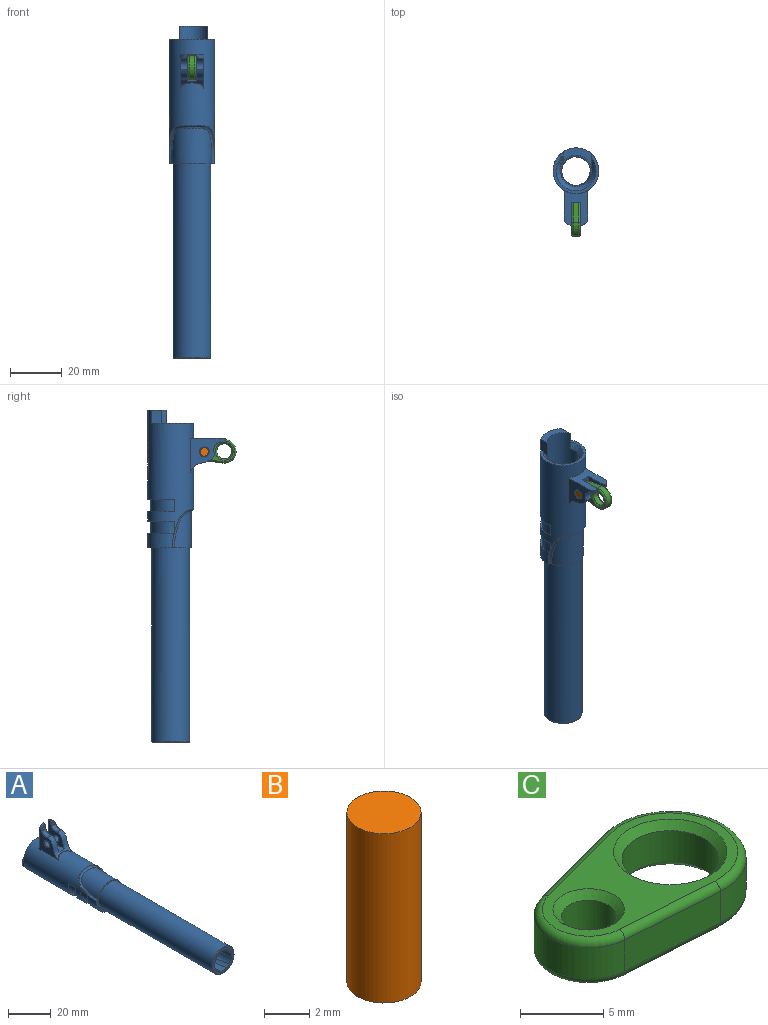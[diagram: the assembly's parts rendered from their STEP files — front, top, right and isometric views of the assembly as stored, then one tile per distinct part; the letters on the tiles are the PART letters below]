
ASSEMBLY  parts=3 mates=2
PART A: 333 faces, bbox 31.5x130.4x32.7 mm
  f0: bspline ~95.71x9.97mm, area 220mm2, adj f16,f17,f18,f23
  f1: bspline ~95.71x9.42mm, area 220mm2, adj f14,f15,f22,f23
  f2: bspline ~95.71x9.97mm, area 220mm2, adj f11,f12,f13,f23
  f3: bspline ~95.71x11mm, area 220mm2, adj f8,f9,f10,f23
  f4: bspline ~95.71x9.42mm, area 220mm2, adj f19,f20,f21,f23
  f5: bspline ~95.71x11mm, area 220mm2, adj f23,f24,f25,f26
  f6: bspline ~14.67x14.67mm, area 9.1mm2, adj f7,f23,f39
  f7: bspline ~14.67x14.67mm, area 9.1mm2, adj f6,f23,f39
  f8: bspline ~95.71x9.97mm, area 14.2mm2, adj f3,f9,f23,f42
  f9: plane 1.95x1.39mm, normal (0,-1,0), area 0.3mm2, adj f3,f8,f10,f42
  f10: bspline ~95.71x9.72mm, area 14.2mm2, adj f3,f9,f23,f42
  f11: bspline ~95.71x8mm, area 14.2mm2, adj f2,f12,f23,f42,f44
  f12: plane 2.28x0.36mm, normal (0,-1,0), area 0.3mm2, adj f2,f11,f13,f42
  f13: bspline ~95.71x9.71mm, area 14.2mm2, adj f2,f12,f23,f42,f43
  f14: bspline ~95.71x9.3mm, area 14.2mm2, adj f1,f15,f23,f42,f43
  f15: plane 2.1x1.12mm, normal (0,-1,0), area 0.3mm2, adj f1,f14,f22,f42
  f16: bspline ~95.71x8mm, area 14.2mm2, adj f0,f17,f23,f42
  f17: plane 2.28x0.36mm, normal (0,-1,0), area 0.3mm2, adj f0,f16,f18,f42
  f18: bspline ~95.71x9.71mm, area 14.2mm2, adj f0,f17,f23,f42
  f19: bspline ~95.71x9.3mm, area 14.2mm2, adj f4,f20,f23,f42
  f20: plane 2.1x1.12mm, normal (0,-1,0), area 0.3mm2, adj f4,f19,f21,f42
  f21: bspline ~95.71x7.31mm, area 14.2mm2, adj f4,f20,f23,f42
  f22: bspline ~95.71x7.31mm, area 14.2mm2, adj f1,f15,f23,f42
  f23: plane 14.17x14.17mm, normal (0,-1,0), area 53mm2, adj f0,f1,f2,f3,f4,f5,f6,f7
  f24: bspline ~95.71x9.97mm, area 14.2mm2, adj f5,f23,f25,f42
  f25: plane 1.95x1.39mm, normal (0,-1,0), area 0.3mm2, adj f5,f24,f26,f42
  f26: bspline ~95.71x9.72mm, area 14.2mm2, adj f5,f23,f25,f42
  f27: cylinder r=8.84mm len=1.49mm, axis (0,-1,0), area 1.3mm2, adj f45,f46,f47,f48,f49
  f28: cylinder r=8.84mm len=0.91mm, axis (0,-1,0), area 0.3mm2, adj f50,f51,f52,f53
  f29: cylinder r=8.84mm len=1.14mm, axis (0,-1,0), area 0.6mm2, adj f54,f55,f56,f57
  f30: cylinder r=8.84mm len=0.96mm, axis (0,-1,0), area 0.4mm2, adj f58,f59,f60,f61
  f31: cylinder r=8.84mm len=0.8mm, axis (0,-1,0), area 0.3mm2, adj f62,f63,f64
  f32: cylinder r=8.84mm len=0.8mm, axis (0,-1,0), area 0.3mm2, adj f65,f66,f67
  f33: cylinder r=8.84mm len=1.03mm, axis (0,-1,0), area 0.5mm2, adj f68,f69,f70,f71
  f34: cylinder r=1mm len=1.76mm, axis (-1,0,0), area 1.3mm2, adj f35,f76,f81
  f35: cylinder r=2.94mm len=2.85mm, axis (-1,0,0), area 3.9mm2, adj f34,f72,f76,f81,f260
  f36: cylinder r=2.94mm len=2.85mm, axis (-1,0,0), area 3.9mm2, adj f37,f74,f77,f79,f263
  f37: cylinder r=1mm len=1.76mm, axis (-1,0,0), area 1.3mm2, adj f36,f77,f79
  f38: bspline ~3.5x2.74mm, area 14.6mm2, adj f75,f79,f80,f81
  f39: cylinder r=7.32mm len=74.75mm, axis (0,1,0), area 3437.8mm2, adj f6,f7,f82
  f40: cylinder r=8.84mm len=1.06mm, axis (0,-1,0), area 0.4mm2, adj f83,f84,f85
  f41: cylinder r=8.84mm len=1.2mm, axis (0,-1,0), area 0.4mm2, adj f86,f87,f88
  f42: cylinder r=5.69mm len=97.7mm, axis (0,1,0), area 2001.4mm2, adj f8,f9,f10,f11,f12,f13,f14,f15
  f43: cylinder r=5.69mm len=65.84mm, axis (0,1,0), area 189mm2, adj f13,f14,f23,f42
  f44: cylinder r=5.69mm len=17.51mm, axis (0,1,0), area 18.9mm2, adj f11,f23,f42
  f45: bspline ~1.09x0.87mm, area 0.3mm2, adj f27,f46,f49,f90
  f46: bspline ~1.16x1mm, area 0.3mm2, adj f27,f45,f47,f90
  f47: bspline ~0.57x0.55mm, area 0.2mm2, adj f27,f46,f48,f90
  f48: bspline ~0.72x0.67mm, area 0.2mm2, adj f27,f47,f49,f90
  f49: bspline ~1.09x0.87mm, area 0.3mm2, adj f27,f45,f48,f90
  f50: bspline ~0.46x0.46mm, area 0.2mm2, adj f28,f51,f53,f91
  f51: bspline ~0.47x0.46mm, area 0.2mm2, adj f28,f50,f52,f91
  f52: bspline ~0.49x0.48mm, area 0.2mm2, adj f28,f51,f53,f91
  f53: bspline ~0.5x0.49mm, area 0.2mm2, adj f28,f50,f52,f91
  f54: bspline ~0.62x0.6mm, area 0.2mm2, adj f29,f55,f57,f91
  f55: bspline ~0.65x0.62mm, area 0.2mm2, adj f29,f54,f56,f91
  f56: bspline ~0.62x0.62mm, area 0.2mm2, adj f29,f55,f57,f91
  f57: bspline ~0.64x0.64mm, area 0.2mm2, adj f29,f54,f56,f91
  f58: bspline ~0.58x0.52mm, area 0.2mm2, adj f30,f59,f61,f98
  f59: bspline ~0.61x0.56mm, area 0.2mm2, adj f30,f58,f60,f98
  f60: bspline ~0.63x0.57mm, area 0.2mm2, adj f30,f59,f61,f98
  f61: bspline ~0.57x0.52mm, area 0.2mm2, adj f30,f58,f60,f98
  f62: plane 0.63x0.23mm, normal (0.9,0,0.44), area 0.2mm2, adj f31,f63,f64,f99
  f63: plane 0.92x0.46mm, normal (0,-1,0), area 0.2mm2, adj f31,f62,f64,f99
  f64: plane 0.92x0.64mm, normal (-0.55,0.79,-0.27), area 0.3mm2, adj f31,f62,f63,f99
  f65: plane 0.63x0.23mm, normal (0.9,0,0.44), area 0.2mm2, adj f32,f66,f67,f100
  f66: plane 0.92x0.46mm, normal (0,-1,0), area 0.2mm2, adj f32,f65,f67,f100
  f67: plane 0.92x0.64mm, normal (-0.55,0.79,-0.27), area 0.3mm2, adj f32,f65,f66,f100
  f68: bspline ~0.59x0.55mm, area 0.2mm2, adj f33,f69,f71,f101
  f69: bspline ~0.59x0.55mm, area 0.2mm2, adj f33,f68,f70,f101
  f70: bspline ~0.57x0.52mm, area 0.2mm2, adj f33,f69,f71,f101
  f71: bspline ~0.57x0.52mm, area 0.2mm2, adj f33,f68,f70,f101
  f72: cylinder r=1mm len=2.85mm, axis (-1,0,0), area 0.8mm2, adj f35,f81,f104,f260
  f73: cylinder r=1.68mm len=3.36mm, axis (1,0,0), area 28mm2, adj f81,f105,f106
  f74: cylinder r=1mm len=2.85mm, axis (-1,0,0), area 0.8mm2, adj f36,f79,f107,f263
  f75: plane 3.5x1.58mm, normal (0,0,1), area 5.5mm2, adj f38,f79,f81,f108
  f76: bspline ~2.85x2.12mm, area 4.6mm2, adj f34,f35,f81,f108,f260
  f77: bspline ~2.89x2.13mm, area 4.6mm2, adj f36,f37,f79,f108,f263
  f78: cylinder r=1.68mm len=3.36mm, axis (1,0,0), area 28mm2, adj f79,f109,f110
  f79: plane 11.85x10.66mm, normal (1,0,0), area 57.5mm2, adj f36,f37,f38,f74,f75,f77,f78,f80
  f80: plane 6.34x3.5mm, normal (0,0,1), area 22.2mm2, adj f38,f79,f81,f111
  f81: plane 11.85x10.66mm, normal (-1,0,0), area 57.5mm2, adj f34,f35,f38,f72,f73,f75,f76,f80
  f82: plane 17.7x16.69mm, normal (0,-1,0), area 51.9mm2, adj f39,f112,f113,f258,f266,f267
  f83: plane 1.22x0.5mm, normal (-0.38,-0.91,-0.18), area 0.3mm2, adj f40,f84,f85,f117
  f84: plane 1.22x0.5mm, normal (-0.38,0.9,-0.19), area 0.3mm2, adj f40,f83,f85,f117
  f85: plane 0.82x0.27mm, normal (0.9,0,0.44), area 0.2mm2, adj f40,f83,f84,f117
  f86: plane 0.68x0.27mm, normal (0.9,0,0.44), area 0.2mm2, adj f41,f87,f88,f119
  f87: plane 1.34x0.48mm, normal (0,-1,0), area 0.3mm2, adj f41,f86,f88,f119
  f88: plane 1.36x0.7mm, normal (-0.51,0.82,-0.25), area 0.4mm2, adj f41,f86,f87,f119
  f89: plane 12.12x12.12mm, normal (0,1,0), area 13.5mm2, adj f42,f120
  f90: cylinder r=8.58mm len=1.83mm, axis (0,-1,0), area 1.9mm2, adj f45,f46,f47,f48,f49,f124,f125,f126
  f91: cylinder r=8.58mm len=1.83mm, axis (0,-1,0), area 1.4mm2, adj f50,f51,f52,f53,f54,f55,f56,f57
  f92: cylinder r=8.58mm len=2.23mm, axis (0,-1,0), area 0.9mm2, adj f137,f138,f139,f140,f141,f142,f143
  f93: cylinder r=8.58mm len=2.23mm, axis (0,-1,0), area 0.9mm2, adj f144,f145,f146,f147,f148,f149,f150
  f94: cylinder r=8.58mm len=2.2mm, axis (0,-1,0), area 1.1mm2, adj f151,f152,f153,f154,f155,f156,f157,f158
  f95: cylinder r=8.58mm len=2.23mm, axis (0,-1,0), area 2.7mm2, adj f159,f160,f161,f162,f163,f164,f165,f166
  f96: cylinder r=8.58mm len=2.23mm, axis (0,-1,0), area 2.2mm2, adj f174,f175,f176,f177,f178,f179,f180,f181
  f97: cylinder r=8.58mm len=2.2mm, axis (0,-1,0), area 1.1mm2, adj f184,f185,f186,f187,f188,f189,f190,f191
  f98: cylinder r=8.58mm len=2.25mm, axis (0,-1,0), area 1.6mm2, adj f58,f59,f60,f61,f192,f193,f194,f195
  f99: cylinder r=8.58mm len=2.2mm, axis (0,-1,0), area 1.4mm2, adj f62,f63,f64,f202,f203,f204,f205,f206
  f100: cylinder r=8.58mm len=2.2mm, axis (0,-1,0), area 1.4mm2, adj f65,f66,f67,f213,f214,f215,f216,f217
  f101: cylinder r=8.58mm len=1.83mm, axis (0,-1,0), area 1.1mm2, adj f68,f69,f70,f71,f224,f225,f226,f227
  f102: cylinder r=8.58mm len=1.83mm, axis (0,-1,0), area 1.3mm2, adj f232,f233,f234,f235,f236,f237,f238,f239
  f103: plane 1.04x0.27mm, normal (-0.9,0,-0.44), area 0.3mm2, adj f117,f252,f253,f323
  f104: cylinder r=2.94mm len=4.3mm, axis (-1,0,0), area 14.6mm2, adj f72,f81,f111,f260
  f105: bspline ~3.76x3.76mm, area 1.7mm2, adj f73,f106,f260
  f106: bspline ~3.76x3.76mm, area 1.7mm2, adj f73,f105,f260
  f107: cylinder r=2.94mm len=4.3mm, axis (-1,0,0), area 14.6mm2, adj f74,f79,f111,f263
  f108: plane 13.52x9.24mm, normal (0,1,0), area 80.9mm2, adj f75,f76,f77,f79,f81,f260,f261,f262
  f109: bspline ~3.76x3.76mm, area 1.7mm2, adj f78,f110,f263
  f110: bspline ~3.76x3.76mm, area 1.7mm2, adj f78,f109,f263
  f111: bspline ~9.36x9.2mm, area 66mm2, adj f79,f80,f81,f104,f107,f259,f260,f263
  f112: cylinder r=7.82mm len=15.38mm, axis (0,-1,0), area 258.8mm2, adj f82,f266
  f113: cylinder r=8.84mm len=17.67mm, axis (0,-1,0), area 166.4mm2, adj f82,f114,f258,f267
  f114: plane 17.77x10.16mm, normal (0,1,0), area 19.9mm2, adj f113,f257,f258,f267,f268
  f115: cylinder r=8.58mm len=2.77mm, axis (0,-1,0), area 0.9mm2, adj f255,f273,f274,f275,f276,f277,f278,f279
  f116: cylinder r=8.58mm len=2.84mm, axis (0,-1,0), area 1.3mm2, adj f280,f281,f282,f283,f284,f285,f286,f287
  f117: cylinder r=8.58mm len=2.77mm, axis (0,-1,0), area 1.4mm2, adj f83,f84,f85,f103,f251,f252,f253,f254
  f118: cylinder r=8.58mm len=2.84mm, axis (0,-1,0), area 1.4mm2, adj f296,f297,f298,f299,f300,f301,f302,f303
  f119: cylinder r=8.58mm len=2.85mm, axis (0,-1,0), area 1.3mm2, adj f86,f87,f88,f250,f310,f311,f312,f313
  f120: cylinder r=6.06mm len=30.5mm, axis (0,1,0), area 987.5mm2, adj f89,f121,f122,f123,f249,f319,f320
  f121: bspline ~15.12x10.86mm, area 56.4mm2, adj f120,f122,f123,f321
  f122: bspline ~4.81x3.72mm, area 6.8mm2, adj f120,f121,f320,f321
  f123: bspline ~8.18x2.53mm, area 16.4mm2, adj f120,f121,f249,f321
  f124: bspline ~1.32x1.01mm, area 0.4mm2, adj f90,f125,f127,f323
  f125: bspline ~1.32x1.01mm, area 0.4mm2, adj f90,f124,f126,f323
  f126: bspline ~1.42x1.2mm, area 0.4mm2, adj f90,f125,f127,f323
  f127: bspline ~1.4x1.19mm, area 0.4mm2, adj f90,f124,f126,f323
  f128: bspline ~0.69x0.67mm, area 0.3mm2, adj f91,f129,f136,f323
  f129: bspline ~0.61x0.57mm, area 0.2mm2, adj f91,f128,f130,f323
  f130: bspline ~0.77x0.7mm, area 0.2mm2, adj f91,f129,f131,f323
  f131: bspline ~0.9x0.83mm, area 0.3mm2, adj f91,f130,f132,f323
  f132: bspline ~0.61x0.47mm, area 0.2mm2, adj f91,f131,f133,f323
  f133: bspline ~0.63x0.63mm, area 0.1mm2, adj f91,f132,f134,f323
  f134: bspline ~0.76x0.69mm, area 0.2mm2, adj f91,f133,f135,f323
  f135: bspline ~0.6x0.56mm, area 0.2mm2, adj f91,f134,f136,f323
  f136: bspline ~0.7x0.65mm, area 0.3mm2, adj f91,f128,f135,f323
  f137: bspline ~0.7x0.63mm, area 0.2mm2, adj f92,f138,f143,f323
  f138: plane 0.38x0.3mm, normal (0,-1,0), area 0.1mm2, adj f92,f137,f139,f323
  f139: bspline ~0.53x0.45mm, area 0.2mm2, adj f92,f138,f140,f323
  f140: plane 1.82x0.79mm, normal (0,-1,0), area 0.5mm2, adj f92,f139,f141,f323
  f141: plane 0.29x0.23mm, normal (-0.9,0,-0.44), area 0.1mm2, adj f92,f140,f142,f323
  f142: plane 2.34x0.89mm, normal (0,1,0), area 0.6mm2, adj f92,f141,f143,f323
  f143: plane 0.24x0.19mm, normal (0.9,0,0.44), area 0.1mm2, adj f92,f137,f142,f323
  f144: bspline ~0.7x0.63mm, area 0.2mm2, adj f93,f145,f150,f323
  f145: plane 0.38x0.3mm, normal (0,-1,0), area 0.1mm2, adj f93,f144,f146,f323
  f146: bspline ~0.53x0.45mm, area 0.2mm2, adj f93,f145,f147,f323
  f147: plane 1.82x0.79mm, normal (0,-1,0), area 0.5mm2, adj f93,f146,f148,f323
  f148: plane 0.29x0.23mm, normal (-0.9,0,-0.44), area 0.1mm2, adj f93,f147,f149,f323
  f149: plane 2.34x0.89mm, normal (0,1,0), area 0.6mm2, adj f93,f148,f150,f323
  f150: plane 0.24x0.19mm, normal (0.9,0,0.44), area 0.1mm2, adj f93,f144,f149,f323
  f151: plane 0.29x0.23mm, normal (-0.9,0,-0.44), area 0.1mm2, adj f94,f152,f158,f323
  f152: bspline ~0.69x0.54mm, area 0.2mm2, adj f94,f151,f153,f323
  f153: bspline ~1.49x1.09mm, area 0.4mm2, adj f94,f152,f154,f323
  f154: plane 0.36x0.28mm, normal (0,1,0), area 0.1mm2, adj f94,f153,f155,f323
  f155: plane 1.47x0.24mm, normal (0.9,0,0.44), area 0.4mm2, adj f94,f154,f156,f323
  f156: plane 0.42x0.29mm, normal (0,-1,0), area 0.1mm2, adj f94,f155,f157,f323
  f157: plane 1.17x0.24mm, normal (-0.9,0,-0.44), area 0.3mm2, adj f94,f156,f158,f323
  f158: bspline ~2.01x1.36mm, area 0.6mm2, adj f94,f151,f157,f323
  f159: plane 1.98x0.83mm, normal (-0.27,-0.95,-0.13), area 0.5mm2, adj f95,f160,f173,f323
  f160: plane 0.34x0.23mm, normal (-0.9,0,-0.44), area 0.1mm2, adj f95,f159,f161,f323
  f161: plane 1.98x0.83mm, normal (-0.27,0.95,-0.13), area 0.5mm2, adj f95,f160,f162,f323
  f162: plane 1.98x0.82mm, normal (0,-1,0), area 0.5mm2, adj f95,f161,f163,f323
  f163: plane 0.32x0.23mm, normal (-0.9,0,-0.44), area 0.1mm2, adj f95,f162,f164,f323
  f164: plane 2.34x0.89mm, normal (0,1,0), area 0.6mm2, adj f95,f163,f165,f323
  f165: plane 0.48x0.24mm, normal (0.9,0,0.44), area 0.1mm2, adj f95,f164,f166,f323
  f166: plane 1.69x0.63mm, normal (0.27,-0.95,0.13), area 0.4mm2, adj f95,f165,f167,f323
  f167: bspline ~0.46x0.42mm, area 0.1mm2, adj f95,f166,f168,f323
  f168: bspline ~0.43x0.41mm, area 0.1mm2, adj f95,f167,f169,f323
  f169: plane 1.71x0.64mm, normal (0.27,0.95,0.13), area 0.4mm2, adj f95,f168,f170,f323
  f170: plane 0.49x0.24mm, normal (0.9,0,0.44), area 0.1mm2, adj f95,f169,f171,f323
  f171: plane 2.34x0.89mm, normal (0,-1,0), area 0.6mm2, adj f95,f170,f172,f323
  f172: plane 0.32x0.23mm, normal (-0.9,0,-0.44), area 0.1mm2, adj f95,f171,f173,f323
  f173: plane 1.98x0.82mm, normal (0,1,0), area 0.5mm2, adj f95,f159,f172,f323
  f174: plane 1.75x1.1mm, normal (-0.49,-0.84,-0.24), area 0.5mm2, adj f96,f175,f183,f323
  f175: plane 0.34x0.23mm, normal (-0.9,0,-0.44), area 0.1mm2, adj f96,f174,f176,f323
  f176: plane 2.34x0.89mm, normal (0,1,0), area 0.6mm2, adj f96,f175,f177,f323
  f177: plane 0.32x0.24mm, normal (0.9,0,0.44), area 0.1mm2, adj f96,f176,f178,f323
  f178: plane 1.8x0.67mm, normal (0,-1,0), area 0.4mm2, adj f96,f177,f179,f323
  f179: plane 1.81x1.11mm, normal (0.49,0.84,0.24), area 0.5mm2, adj f96,f178,f180,f323
  f180: plane 0.34x0.24mm, normal (0.9,0,0.44), area 0.1mm2, adj f96,f179,f181,f323
  f181: plane 2.34x0.89mm, normal (0,-1,0), area 0.6mm2, adj f96,f180,f182,f323
  f182: plane 0.32x0.23mm, normal (-0.9,0,-0.44), area 0.1mm2, adj f96,f181,f183,f323
  f183: plane 1.75x0.77mm, normal (0,1,0), area 0.4mm2, adj f96,f174,f182,f323
  f184: plane 0.29x0.23mm, normal (-0.9,0,-0.44), area 0.1mm2, adj f97,f185,f191,f323
  f185: bspline ~0.69x0.54mm, area 0.2mm2, adj f97,f184,f186,f323
  f186: bspline ~1.49x1.09mm, area 0.4mm2, adj f97,f185,f187,f323
  f187: plane 0.36x0.28mm, normal (0,1,0), area 0.1mm2, adj f97,f186,f188,f323
  f188: plane 1.47x0.24mm, normal (0.9,0,0.44), area 0.4mm2, adj f97,f187,f189,f323
  f189: plane 0.42x0.29mm, normal (0,-1,0), area 0.1mm2, adj f97,f188,f190,f323
  f190: plane 1.17x0.24mm, normal (-0.9,0,-0.44), area 0.3mm2, adj f97,f189,f191,f323
  f191: bspline ~2.01x1.36mm, area 0.6mm2, adj f97,f184,f190,f323
  f192: bspline ~1.22x0.96mm, area 0.4mm2, adj f98,f193,f201,f323
  f193: bspline ~0.88x0.75mm, area 0.3mm2, adj f98,f192,f194,f323
  f194: bspline ~0.84x0.68mm, area 0.3mm2, adj f98,f193,f195,f323
  f195: bspline ~0.53x0.4mm, area 0.2mm2, adj f98,f194,f196,f323
  f196: bspline ~0.27x0.17mm, area 0mm2, adj f98,f195,f197,f323
  f197: bspline ~0.88x0.67mm, area 0.3mm2, adj f98,f196,f198,f323
  f198: bspline ~0.45x0.41mm, area 0.1mm2, adj f98,f197,f199,f323
  f199: plane 0.3x0.25mm, normal (0.89,-0.1,0.44), area 0.1mm2, adj f98,f198,f200,f323
  f200: bspline ~0.66x0.63mm, area 0.2mm2, adj f98,f199,f201,f323
  f201: bspline ~1.26x0.88mm, area 0.4mm2, adj f98,f192,f200,f323
  f202: plane 0.29x0.23mm, normal (-0.9,0,-0.44), area 0.1mm2, adj f99,f203,f212,f323
  f203: plane 0.39x0.33mm, normal (0,1,0), area 0.1mm2, adj f99,f202,f204,f323
  f204: plane 0.29x0.23mm, normal (0.9,0,0.44), area 0.1mm2, adj f99,f203,f205,f323
  f205: plane 1.51x0.58mm, normal (0,1,0), area 0.4mm2, adj f99,f204,f206,f323
  f206: plane 0.24x0.21mm, normal (0.9,0,0.44), area 0.1mm2, adj f99,f205,f207,f323
  f207: plane 1.52x1.09mm, normal (0.55,-0.79,0.27), area 0.5mm2, adj f99,f206,f208,f323
  f208: plane 0.39x0.33mm, normal (0,-1,0), area 0.1mm2, adj f99,f207,f209,f323
  f209: plane 1x0.23mm, normal (-0.9,0,-0.44), area 0.3mm2, adj f99,f208,f210,f323
  f210: plane 0.63x0.44mm, normal (0,-1,0), area 0.1mm2, adj f99,f209,f211,f323
  f211: plane 0.29x0.23mm, normal (-0.9,0,-0.44), area 0.1mm2, adj f99,f210,f212,f323
  f212: plane 0.63x0.44mm, normal (0,1,0), area 0.1mm2, adj f99,f202,f211,f323
  f213: plane 0.29x0.23mm, normal (-0.9,0,-0.44), area 0.1mm2, adj f100,f214,f223,f323
  f214: plane 0.39x0.33mm, normal (0,1,0), area 0.1mm2, adj f100,f213,f215,f323
  f215: plane 0.29x0.23mm, normal (0.9,0,0.44), area 0.1mm2, adj f100,f214,f216,f323
  f216: plane 1.51x0.58mm, normal (0,1,0), area 0.4mm2, adj f100,f215,f217,f323
  f217: plane 0.24x0.21mm, normal (0.9,0,0.44), area 0.1mm2, adj f100,f216,f218,f323
  f218: plane 1.52x1.09mm, normal (0.55,-0.79,0.27), area 0.5mm2, adj f100,f217,f219,f323
  f219: plane 0.39x0.33mm, normal (0,-1,0), area 0.1mm2, adj f100,f218,f220,f323
  f220: plane 1x0.23mm, normal (-0.9,0,-0.44), area 0.3mm2, adj f100,f219,f221,f323
  f221: plane 0.63x0.44mm, normal (0,-1,0), area 0.1mm2, adj f100,f220,f222,f323
  f222: plane 0.29x0.23mm, normal (-0.9,0,-0.44), area 0.1mm2, adj f100,f221,f223,f323
  f223: plane 0.63x0.44mm, normal (0,1,0), area 0.1mm2, adj f100,f213,f222,f323
  f224: bspline ~0.81x0.71mm, area 0.3mm2, adj f101,f225,f231,f323
  f225: bspline ~0.8x0.73mm, area 0.3mm2, adj f101,f224,f226,f323
  f226: bspline ~0.82x0.71mm, area 0.3mm2, adj f101,f225,f227,f323
  f227: bspline ~0.26x0.24mm, area 0.1mm2, adj f101,f226,f228,f323
  f228: plane 0.98x0.8mm, normal (0.51,-0.83,0.25), area 0.3mm2, adj f101,f227,f229,f323
  f229: plane 0.35x0.2mm, normal (-0.74,-0.57,-0.36), area 0.1mm2, adj f101,f228,f230,f323
  f230: plane 1.08x0.88mm, normal (-0.51,0.83,-0.25), area 0.3mm2, adj f101,f229,f231,f323
  f231: bspline ~0.81x0.71mm, area 0.2mm2, adj f101,f224,f230,f323
  f232: bspline ~0.59x0.49mm, area 0.2mm2, adj f102,f233,f248,f323
  f233: plane 0.4x0.3mm, normal (0,-1,0), area 0.1mm2, adj f102,f232,f234,f323
  f234: bspline ~0.7x0.63mm, area 0.3mm2, adj f102,f233,f235,f323
  f235: bspline ~0.65x0.64mm, area 0.2mm2, adj f102,f234,f236,f323
  f236: bspline ~0.39x0.35mm, area 0.1mm2, adj f102,f235,f237,f323
  f237: bspline ~0.5x0.46mm, area 0.1mm2, adj f102,f236,f238,f323
  f238: plane 0.24x0.21mm, normal (0.9,0,0.44), area 0.1mm2, adj f102,f237,f239,f323
  f239: bspline ~0.85x0.8mm, area 0.3mm2, adj f102,f238,f240,f323
  f240: bspline ~0.92x0.85mm, area 0.3mm2, adj f102,f239,f241,f323
  f241: bspline ~0.55x0.55mm, area 0.1mm2, adj f102,f240,f242,f323
  f242: bspline ~0.38x0.32mm, area 0.1mm2, adj f102,f241,f243,f323
  f243: bspline ~0.59x0.55mm, area 0.1mm2, adj f102,f242,f244,f323
  f244: bspline ~0.71x0.67mm, area 0.3mm2, adj f102,f243,f245,f323
  f245: bspline ~0.69x0.68mm, area 0.3mm2, adj f102,f244,f246,f323
  f246: plane 0.23x0.21mm, normal (-0.9,0,-0.44), area 0.1mm2, adj f102,f245,f247,f323
  f247: bspline ~0.48x0.46mm, area 0.2mm2, adj f102,f246,f248,f323
  f248: bspline ~0.47x0.46mm, area 0.2mm2, adj f102,f232,f247,f323
  f249: plane 7.53x5.48mm, normal (1,0,0), area 29.6mm2, adj f120,f123,f319,f321,f323
  f250: plane 0.25x0.21mm, normal (-0.9,0,-0.44), area 0.1mm2, adj f119,f310,f318,f323
  f251: plane 0.25x0.22mm, normal (-0.9,0,-0.44), area 0.1mm2, adj f117,f252,f295,f323
  f252: plane 0.96x0.35mm, normal (-0.39,0.9,-0.19), area 0.2mm2, adj f103,f117,f251,f323
  f253: plane 0.96x0.34mm, normal (-0.38,-0.91,-0.18), area 0.2mm2, adj f103,f117,f254,f323
  f254: plane 0.25x0.22mm, normal (-0.9,0,-0.44), area 0.1mm2, adj f117,f253,f293,f323
  f255: plane 0.25x0.21mm, normal (-0.9,0,-0.44), area 0.1mm2, adj f115,f273,f279,f323
  f256: bspline ~9.43x9.35mm, area 66.6mm2, adj f270,f271,f272,f323
  f257: bspline ~9.43x9.35mm, area 66.4mm2, adj f114,f258,f268,f269,f323
  f258: bspline ~14.78x7.94mm, area 5.4mm2, adj f82,f113,f114,f257,f266,f323
  f259: cylinder r=1mm len=0.62mm, axis (-1,0,0), area 0.1mm2, adj f111,f260,f265,f323
  f260: plane 13.18x11.5mm, normal (1,0,0), area 81.1mm2, adj f35,f72,f76,f104,f105,f106,f108,f111
  f261: bspline ~4.68x1.41mm, area 0.8mm2, adj f108,f260,f262,f323
  f262: bspline ~4.68x1.41mm, area 0.8mm2, adj f108,f261,f263,f323
  f263: plane 13.18x11.5mm, normal (-1,0,0), area 81.1mm2, adj f36,f74,f77,f107,f108,f109,f110,f111
  f264: cylinder r=1mm len=0.62mm, axis (-1,0,0), area 0.1mm2, adj f111,f263,f265,f323
  f265: bspline ~8.83x1.69mm, area 0.7mm2, adj f111,f259,f264,f323
  f266: bspline ~17.36x14.71mm, area 59mm2, adj f82,f112,f258,f267,f323
  f267: bspline ~14.78x7.94mm, area 5.4mm2, adj f82,f113,f114,f266,f268,f323
  f268: bspline ~9.43x9.35mm, area 66.4mm2, adj f114,f257,f267,f269,f323
  f269: plane 17.81x10.57mm, normal (0,-1,0), area 19.9mm2, adj f257,f268,f323
  f270: plane 17.81x10.57mm, normal (0,1,0), area 19.9mm2, adj f256,f271,f323
  f271: bspline ~9.43x9.35mm, area 66.6mm2, adj f256,f270,f272,f323
  f272: plane 17.81x10.57mm, normal (0,-1,0), area 19.9mm2, adj f256,f271,f323
  f273: plane 2.59x0.62mm, normal (0,1,0), area 0.6mm2, adj f115,f255,f274,f323
  f274: plane 0.5x0.31mm, normal (-0.9,0,-0.44), area 0.2mm2, adj f115,f273,f275,f323
  f275: plane 0.46x0.41mm, normal (0,1,0), area 0.1mm2, adj f115,f274,f276,f323
  f276: plane 1.2x0.32mm, normal (0.9,0,0.44), area 0.4mm2, adj f115,f275,f277,f323
  f277: plane 0.46x0.41mm, normal (0,-1,0), area 0.1mm2, adj f115,f276,f278,f323
  f278: plane 0.5x0.31mm, normal (-0.9,0,-0.44), area 0.2mm2, adj f115,f277,f279,f323
  f279: plane 2.59x0.62mm, normal (0,-1,0), area 0.6mm2, adj f115,f255,f278,f323
  f280: bspline ~1.23x1.17mm, area 0.4mm2, adj f116,f281,f292,f323
  f281: plane 1.86x0.67mm, normal (0,1,0), area 0.4mm2, adj f116,f280,f282,f323
  f282: plane 0.32x0.21mm, normal (0.9,0,0.44), area 0.1mm2, adj f116,f281,f283,f323
  f283: plane 1.85x0.67mm, normal (0,-1,0), area 0.4mm2, adj f116,f282,f284,f323
  f284: bspline ~0.62x0.55mm, area 0.1mm2, adj f116,f283,f285,f323
  f285: bspline ~0.63x0.57mm, area 0.2mm2, adj f116,f284,f286,f323
  f286: bspline ~0.67x0.63mm, area 0.2mm2, adj f116,f285,f287,f323
  f287: bspline ~0.58x0.49mm, area 0.1mm2, adj f116,f286,f288,f323
  f288: plane 1.86x0.68mm, normal (0,1,0), area 0.4mm2, adj f116,f287,f289,f323
  f289: plane 0.32x0.21mm, normal (0.9,0,0.44), area 0.1mm2, adj f116,f288,f290,f323
  f290: plane 1.87x0.68mm, normal (0,-1,0), area 0.4mm2, adj f116,f289,f291,f323
  f291: bspline ~0.74x0.7mm, area 0.1mm2, adj f116,f290,f292,f323
  f292: bspline ~0.72x0.7mm, area 0.3mm2, adj f116,f280,f291,f323
  f293: plane 2.89x1.06mm, normal (0.38,0.91,0.18), area 0.8mm2, adj f117,f254,f294,f323
  f294: plane 0.32x0.16mm, normal (0.9,0,0.44), area 0mm2, adj f117,f293,f295,f323
  f295: plane 2.89x1.08mm, normal (0.39,-0.9,0.19), area 0.8mm2, adj f117,f251,f294,f323
  f296: bspline ~1.05x1.01mm, area 0.4mm2, adj f118,f297,f309,f323
  f297: bspline ~1.07x1.04mm, area 0.4mm2, adj f118,f296,f298,f323
  f298: bspline ~0.34x0.27mm, area 0.1mm2, adj f118,f297,f299,f323
  f299: plane 0.91x0.48mm, normal (-0.18,0.98,-0.09), area 0.2mm2, adj f118,f298,f300,f323
  f300: plane 0.78x0.31mm, normal (-0.9,0,-0.44), area 0.3mm2, adj f118,f299,f301,f323
  f301: plane 0.46x0.41mm, normal (0,1,0), area 0.1mm2, adj f118,f300,f302,f323
  f302: plane 0.94x0.32mm, normal (0.9,0,0.44), area 0.3mm2, adj f118,f301,f303,f323
  f303: plane 1.59x0.65mm, normal (0.18,-0.98,0.09), area 0.4mm2, adj f118,f302,f304,f323
  f304: bspline ~0.51x0.41mm, area 0.2mm2, adj f118,f303,f305,f323
  f305: bspline ~0.8x0.73mm, area 0.3mm2, adj f118,f304,f306,f323
  f306: bspline ~0.81x0.8mm, area 0.3mm2, adj f118,f305,f307,f323
  f307: bspline ~0.65x0.6mm, area 0.2mm2, adj f118,f306,f308,f323
  f308: plane 0.26x0.21mm, normal (0.9,0,0.44), area 0.1mm2, adj f118,f307,f309,f323
  f309: bspline ~0.86x0.85mm, area 0.3mm2, adj f118,f296,f308,f323
  f310: plane 0.72x0.28mm, normal (0,1,0), area 0.2mm2, adj f119,f250,f311,f323
  f311: plane 0.26x0.26mm, normal (-0.9,0,-0.44), area 0.1mm2, adj f119,f310,f312,f323
  f312: plane 0.4x0.29mm, normal (0,1,0), area 0.1mm2, adj f119,f311,f313,f323
  f313: plane 0.27x0.26mm, normal (0.9,0,0.44), area 0.1mm2, adj f119,f312,f314,f323
  f314: plane 2.11x0.72mm, normal (0,1,0), area 0.5mm2, adj f119,f313,f315,f323
  f315: plane 0.32x0.16mm, normal (0.9,0,0.44), area 0mm2, adj f119,f314,f316,f323
  f316: plane 2.38x1.25mm, normal (0.51,-0.82,0.25), area 0.7mm2, adj f119,f315,f317,f323
  f317: plane 1.08x0.26mm, normal (-0.9,0,-0.44), area 0.3mm2, adj f119,f316,f318,f323
  f318: plane 0.72x0.28mm, normal (0,-1,0), area 0.2mm2, adj f119,f250,f317,f323
  f319: plane 10.72x7.27mm, normal (0,1,0), area 33.8mm2, adj f120,f249,f320,f323
  f320: plane 7.1x3.76mm, normal (-1,0,0), area 21.6mm2, adj f120,f122,f319,f321,f323
  f321: plane 19.87x18.41mm, normal (0,1,0), area 44.5mm2, adj f121,f122,f123,f249,f320,f323
  f322: cylinder r=8.84mm len=2.32mm, axis (0,-1,0), area 2.3mm2, adj f324,f325,f326,f327
  f323: cylinder r=8.84mm len=46.21mm, axis (0,-1,0), area 1788.2mm2, adj f103,f124,f125,f126,f127,f128,f129,f130
  f324: bspline ~1.41x1.35mm, area 0.5mm2, adj f322,f325,f327,f332
  f325: bspline ~1.43x1.37mm, area 0.5mm2, adj f322,f324,f326,f332
  f326: bspline ~1.25x1.21mm, area 0.5mm2, adj f322,f325,f327,f332
  f327: bspline ~1.25x1.21mm, area 0.5mm2, adj f322,f324,f326,f332
  f328: bspline ~1.74x1.68mm, area 0.5mm2, adj f323,f329,f331,f332
  f329: bspline ~1.74x1.68mm, area 0.5mm2, adj f323,f328,f330,f332
  f330: bspline ~1.52x1.42mm, area 0.6mm2, adj f323,f329,f331,f332
  f331: bspline ~1.5x1.41mm, area 0.5mm2, adj f323,f328,f330,f332
  f332: cylinder r=8.58mm len=2.92mm, axis (0,-1,0), area 1.2mm2, adj f324,f325,f326,f327,f328,f329,f330,f331
PART B: 3 faces, bbox 3.3x3.3x9.2 mm
  f0: plane 3.29x3.29mm, normal (0,0,-1), area 8.5mm2, adj f2
  f1: plane 3.29x3.29mm, normal (0,0,1), area 8.5mm2, adj f2
  f2: cylinder r=1.65mm len=9.2mm, axis (0,0,-1), area 95.1mm2, adj f0,f1
PART C: 20 faces, bbox 16.2x9.8x3.3 mm
  f0: plane 7.63x2.3mm, normal (-0.06,-1,0), area 17.6mm2, adj f1,f2,f8,f12
  f1: cylinder r=4.55mm len=9.1mm, axis (0,0,-1), area 36.3mm2, adj f0,f4,f9,f13
  f2: cylinder r=3.29mm len=6.46mm, axis (0,0,-1), area 21.3mm2, adj f0,f4,f10,f14
  f3: cylinder r=2.91mm len=5.82mm, axis (0,0,-1), area 42.1mm2, adj f17,f18
  f4: plane 7.37x2.3mm, normal (-0.26,0.97,0), area 17.6mm2, adj f1,f2,f11,f15
  f5: cylinder r=1.65mm len=3.3mm, axis (0,0,-1), area 23.8mm2, adj f16,f19
  f6: plane 14.54x8.1mm, normal (0,0,-1), area 40.6mm2, adj f12,f13,f14,f15,f16,f17
  f7: plane 14.54x8.1mm, normal (0,0,1), area 40.6mm2, adj f8,f9,f10,f11,f18,f19
  f8: cylinder r=0.5mm len=7.66mm, axis (-1,0.06,0), area 6mm2, adj f0,f7,f9,f10
  f9: torus R=4.05mm, axis (0,0,1), area 11.9mm2, adj f1,f7,f8,f11
  f10: torus R=2.79mm, axis (0,0,1), area 6.9mm2, adj f2,f7,f8,f11
  f11: cylinder r=0.5mm len=7.5mm, axis (-0.97,-0.26,0), area 6mm2, adj f4,f7,f9,f10
  f12: cylinder r=0.5mm len=7.66mm, axis (1,-0.06,0), area 6mm2, adj f0,f6,f13,f14
  f13: torus R=4.05mm, axis (0,0,1), area 11.9mm2, adj f1,f6,f12,f15
  f14: torus R=2.79mm, axis (0,0,1), area 6.9mm2, adj f2,f6,f12,f15
  f15: cylinder r=0.5mm len=7.5mm, axis (0.97,0.26,0), area 6mm2, adj f4,f6,f13,f14
  f16: cone r=1.65mm half-angle=45deg, axis (0,0,-1), area 8.4mm2, adj f5,f6
  f17: cone r=2.91mm half-angle=45deg, axis (0,0,-1), area 14mm2, adj f3,f6
  f18: cone r=2.91mm half-angle=45deg, axis (0,0,1), area 14mm2, adj f3,f7
  f19: cone r=2.15mm half-angle=45deg, axis (0,0,1), area 8.4mm2, adj f5,f7
PLACE A rot(axis=(1,0,0),90deg) t=(0,0,-156.6)mm fixed
PLACE B rot(axis=(0,1,0),90deg) t=(-4.6,-12.92,-16.16)mm
PLACE C rot(axis=(-0.6,0.53,-0.6),124.2deg) t=(-1.65,-20.38,-20.58)mm
MATE fastened B.f2 <-> A.f78  axis (-1,0,0) through (-4.6,-12.92,-16.16)mm
MATE revolute C.f16 <-> B.f2  axis (-1,0,0) through (0,-12.92,-16.16)mm
